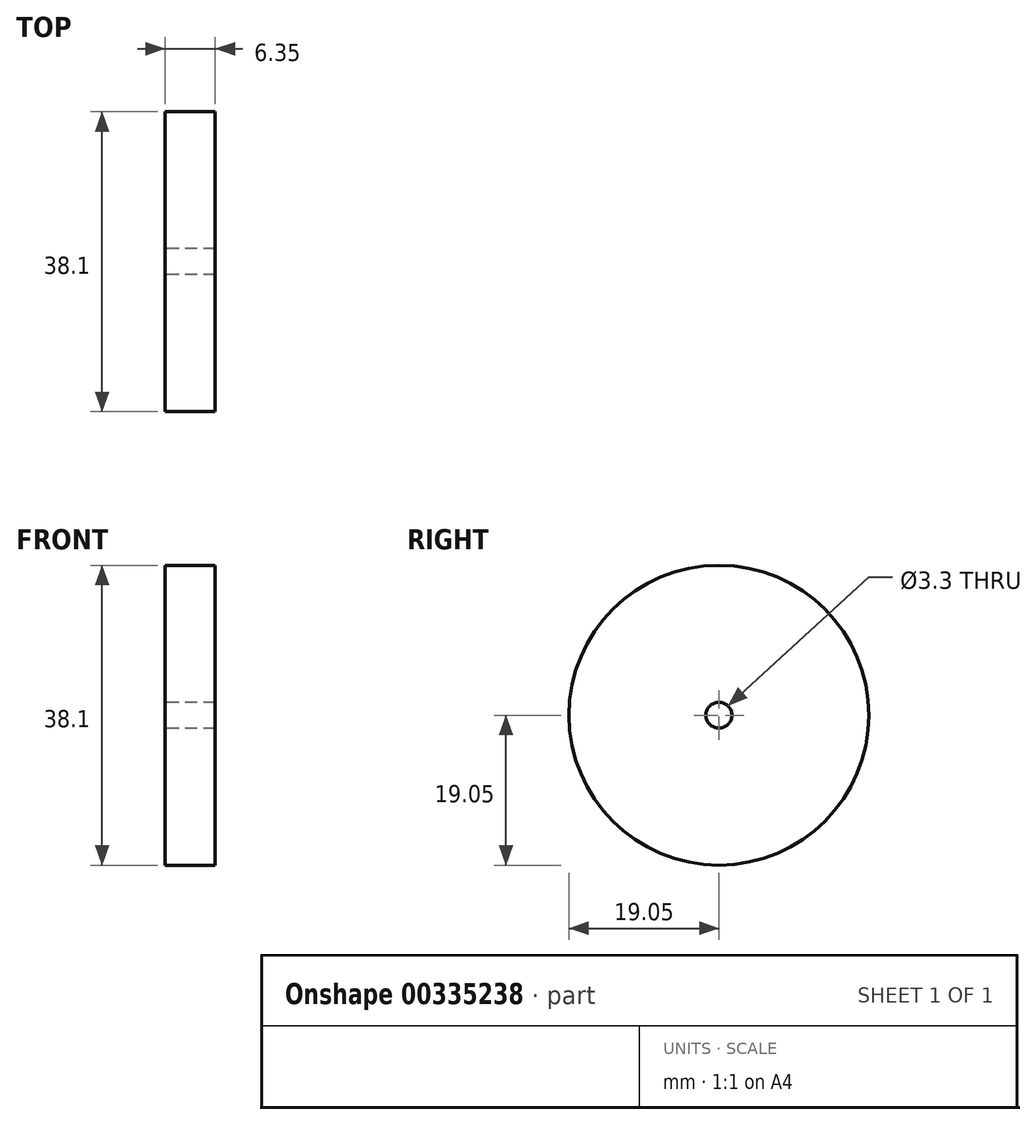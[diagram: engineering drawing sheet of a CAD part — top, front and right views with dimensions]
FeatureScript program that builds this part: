
annotation { "Feature Type Name" : "Feature", "Feature Type Description" : "" }
export const myFeature = defineFeature(function(context is Context, id is Id, definition is map)
    precondition{}
    {
        {
            var Q0;
            Q0=qCreatedBy(makeId("Right.planeOp"),FACE);
            var sketch = newSketch(context, id + "F0", { "sketchPlane" : qUnion([Q0])});
            skCircle(sketch, "E0", {"center": v(0, 0) * mm, "radius": 19.05 * mm});
            skCircle(sketch, "E1", {"center": v(0, 0) * mm, "radius": 1.65 * mm});
            skSolve(sketch);
        }
        {
            var Q0;
            Q0=makeQuery(id+"F0.imprint","IMPRINT",FACE,{"disambiguationData":[TD([[makeQuery(id+"F0.imprint","IMPRINT",EDGE,{"derivedFrom":sQuery(id+"F0.wireOp",EDGE,"E0")}),1.0]])]});
            extrude(context, id + "F1", {"entities" : qUnion([Q0]), "depth" : 6.35 * mm});
        }
    });
